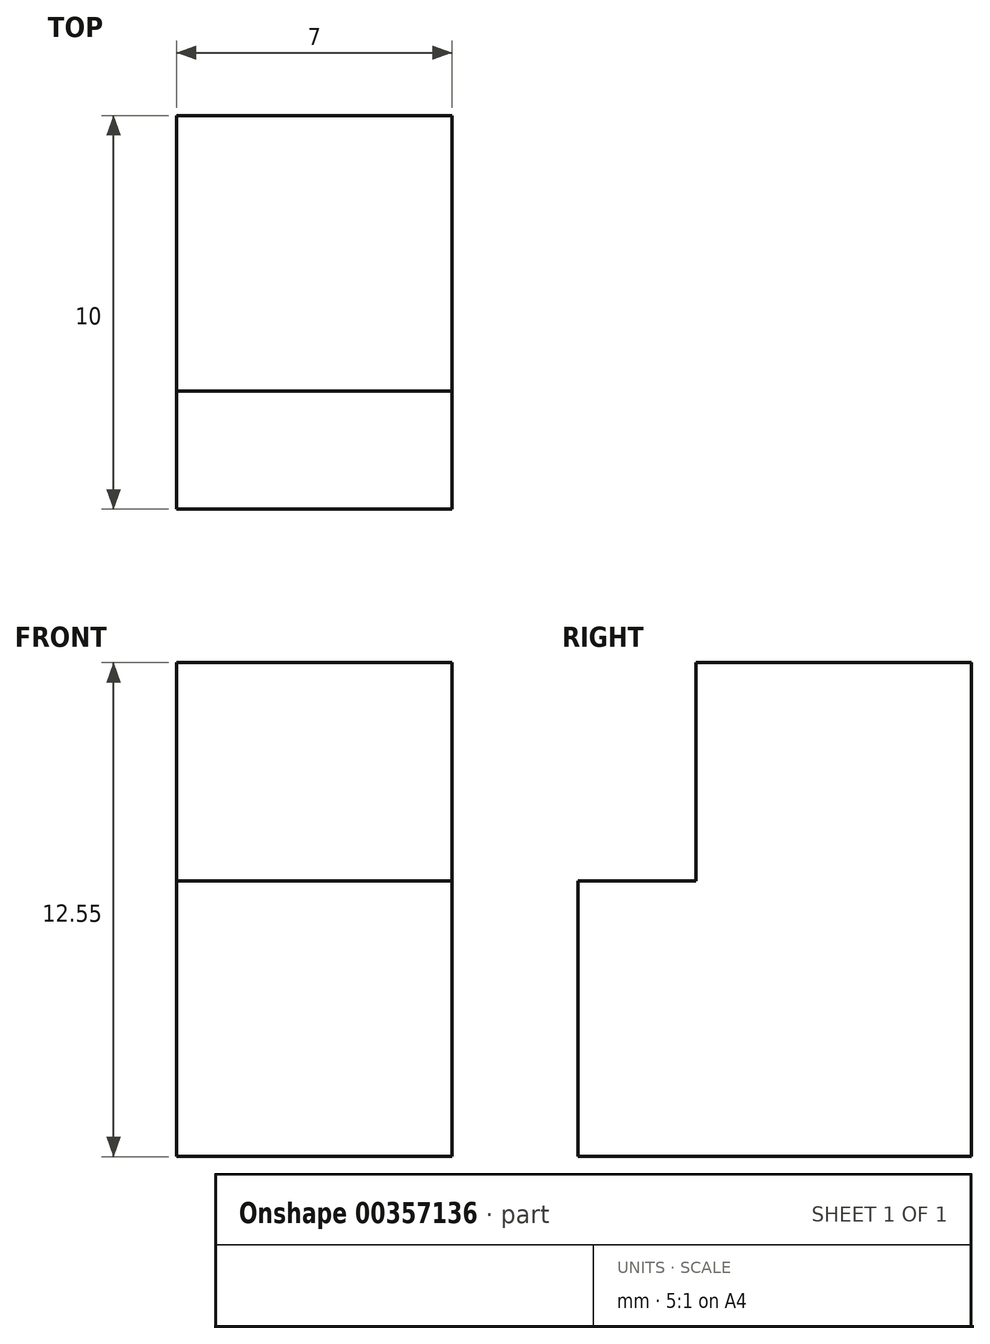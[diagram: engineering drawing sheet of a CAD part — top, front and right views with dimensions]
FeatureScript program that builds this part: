
annotation { "Feature Type Name" : "Feature", "Feature Type Description" : "" }
export const myFeature = defineFeature(function(context is Context, id is Id, definition is map)
    precondition{}
    {
        {
            var Q0;
            Q0=qCreatedBy(makeId("Front.planeOp"),FACE);
            var sketch = newSketch(context, id + "F0", { "sketchPlane" : qUnion([Q0])});
            skLineSegment(sketch, "E0.bottom", {"start": v(3.5, -3) * mm, "end": v(-3.5, -3) * mm});
            skLineSegment(sketch, "E0.top", {"start": v(3.5, 3) * mm, "end": v(-3.5, 3) * mm});
            skLineSegment(sketch, "E0.left", {"start": v(3.5, -3) * mm, "end": v(3.5, 3) * mm});
            skLineSegment(sketch, "E0.right", {"start": v(-3.5, -3) * mm, "end": v(-3.5, 3) * mm});
            skPoint(sketch, "E0.middle", {"position": v(0, 0) * mm});
            skSolve(sketch);
        }
        {
            var Q0;
            Q0=qCreatedBy(makeId("Front.planeOp"),FACE);
            var sketch = newSketch(context, id + "F1", { "sketchPlane" : qUnion([Q0])});
            skLineSegment(sketch, "E1.bottom", {"start": v(-3.5, -9.55) * mm, "end": v(3.5, -9.55) * mm});
            skLineSegment(sketch, "E1.top", {"start": v(-3.5, -2.55) * mm, "end": v(3.5, -2.55) * mm});
            skLineSegment(sketch, "E1.left", {"start": v(-3.5, -9.55) * mm, "end": v(-3.5, -2.55) * mm});
            skLineSegment(sketch, "E1.right", {"start": v(3.5, -9.55) * mm, "end": v(3.5, -2.55) * mm});
            skPoint(sketch, "E1.middle", {"position": v(0, -6.05) * mm});
            skSolve(sketch);
        }
        {
            var Q0;
            Q0 = qSketchRegion(id + "F0", true);
            extrude(context, id + "F2", {"entities" : qUnion([Q0]), "depth" : 7 * mm});
        }
        {
            var Q0;
            Q0 = qSketchRegion(id + "F1", true);
            extrude(context, id + "F3", {"entities" : qUnion([Q0]), "operationType" : NewBodyOperationType.ADD, "depth" : 10 * mm});
        }
    });
